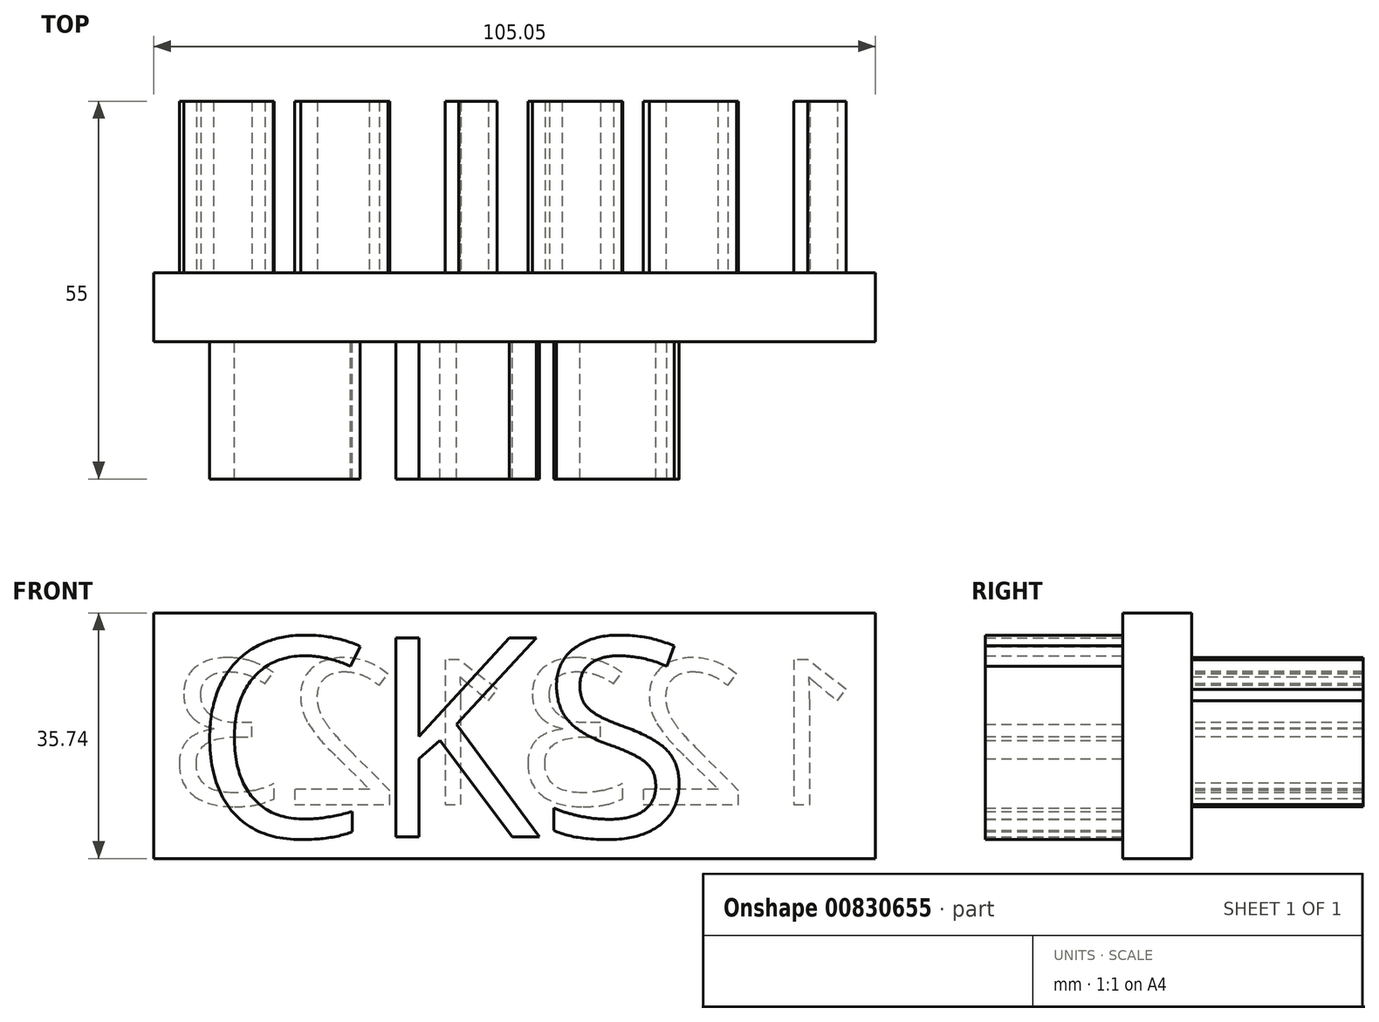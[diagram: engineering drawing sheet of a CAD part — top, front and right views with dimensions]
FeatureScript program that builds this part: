
annotation { "Feature Type Name" : "Feature", "Feature Type Description" : "" }
export const myFeature = defineFeature(function(context is Context, id is Id, definition is map)
    precondition{}
    {
        {
            var Q0;
            Q0=qCreatedBy(makeId("Front.planeOp"),FACE);
            var sketch = newSketch(context, id + "F0", { "sketchPlane" : qUnion([Q0])});
            skLineSegment(sketch, "E0.bottom", {"start": v(0, 0) * mm, "end": v(105.05, 0) * mm});
            skLineSegment(sketch, "E0.top", {"start": v(0, 35.74) * mm, "end": v(105.05, 35.74) * mm});
            skLineSegment(sketch, "E0.left", {"start": v(0, 0) * mm, "end": v(0, 35.74) * mm});
            skLineSegment(sketch, "E0.right", {"start": v(105.05, 0) * mm, "end": v(105.05, 35.74) * mm});
            skSolve(sketch);
        }
        {
            var Q0;
            Q0=makeQuery(id+"F0.imprint","IMPRINT",FACE,{"disambiguationData":[TD([[makeQuery(id+"F0.imprint","IMPRINT",EDGE,{"derivedFrom":sQuery(id+"F0.wireOp",EDGE,"E0.bottom")}),1.0]])]});
            extrude(context, id + "F1", {"entities" : qUnion([Q0]), "depth" : 10 * mm, "offsetDistance" : 25 * mm});
        }
        {
            var Q0;
            Q0=makeQuery(id+"F1.opExtrude","CAP_FACE",FACE,{"disambiguationData":[OSD([sQuery(id+"F0.wireOp",EDGE,"E0.bottom"),sQuery(id+"F0.wireOp",EDGE,"E0.top"),sQuery(id+"F0.wireOp",EDGE,"E0.left"),sQuery(id+"F0.wireOp",EDGE,"E0.right")])],"isStart":false});
            var sketch = newSketch(context, id + "F2", { "sketchPlane" : qUnion([Q0])});
            skText(sketch, "E1", { "text": "CKS", "fontName": "OpenSans-Regular.ttf"});
            const initialGuessF2  = {"E1": [0.00567, 0.00315, 1, 0, 0.0292]};
            skSetInitialGuess(sketch, initialGuessF2);
            skSolve(sketch);
        }
        {
            var Q0;
            Q0 = qSketchRegion(id + "F2", true);
            extrude(context, id + "F3", {"entities" : qUnion([Q0]), "operationType" : NewBodyOperationType.ADD, "depth" : 20 * mm, "offsetDistance" : 25 * mm});
        }
        {
            var Q0;
            Q0=makeQuery(id+"F1.opExtrude","CAP_FACE",FACE,{"disambiguationData":[OSD([sQuery(id+"F0.wireOp",EDGE,"E0.bottom"),sQuery(id+"F0.wireOp",EDGE,"E0.top"),sQuery(id+"F0.wireOp",EDGE,"E0.left"),sQuery(id+"F0.wireOp",EDGE,"E0.right")])],"isStart":true});
            var sketch = newSketch(context, id + "F4", { "sketchPlane" : qUnion([Q0])});
            skText(sketch, "E2", { "text": "123123", "fontName": "OpenSans-Regular.ttf"});
            const initialGuessF4  = {"E2": [-0.10346, 0.00782, 1, 0, 0.0213]};
            skSetInitialGuess(sketch, initialGuessF4);
            skSolve(sketch);
        }
        {
            var Q0;
            Q0 = qSketchRegion(id + "F4", true);
            extrude(context, id + "F5", {"entities" : qUnion([Q0]), "operationType" : NewBodyOperationType.ADD, "depth" : 25 * mm, "offsetDistance" : 25 * mm});
        }
    });
